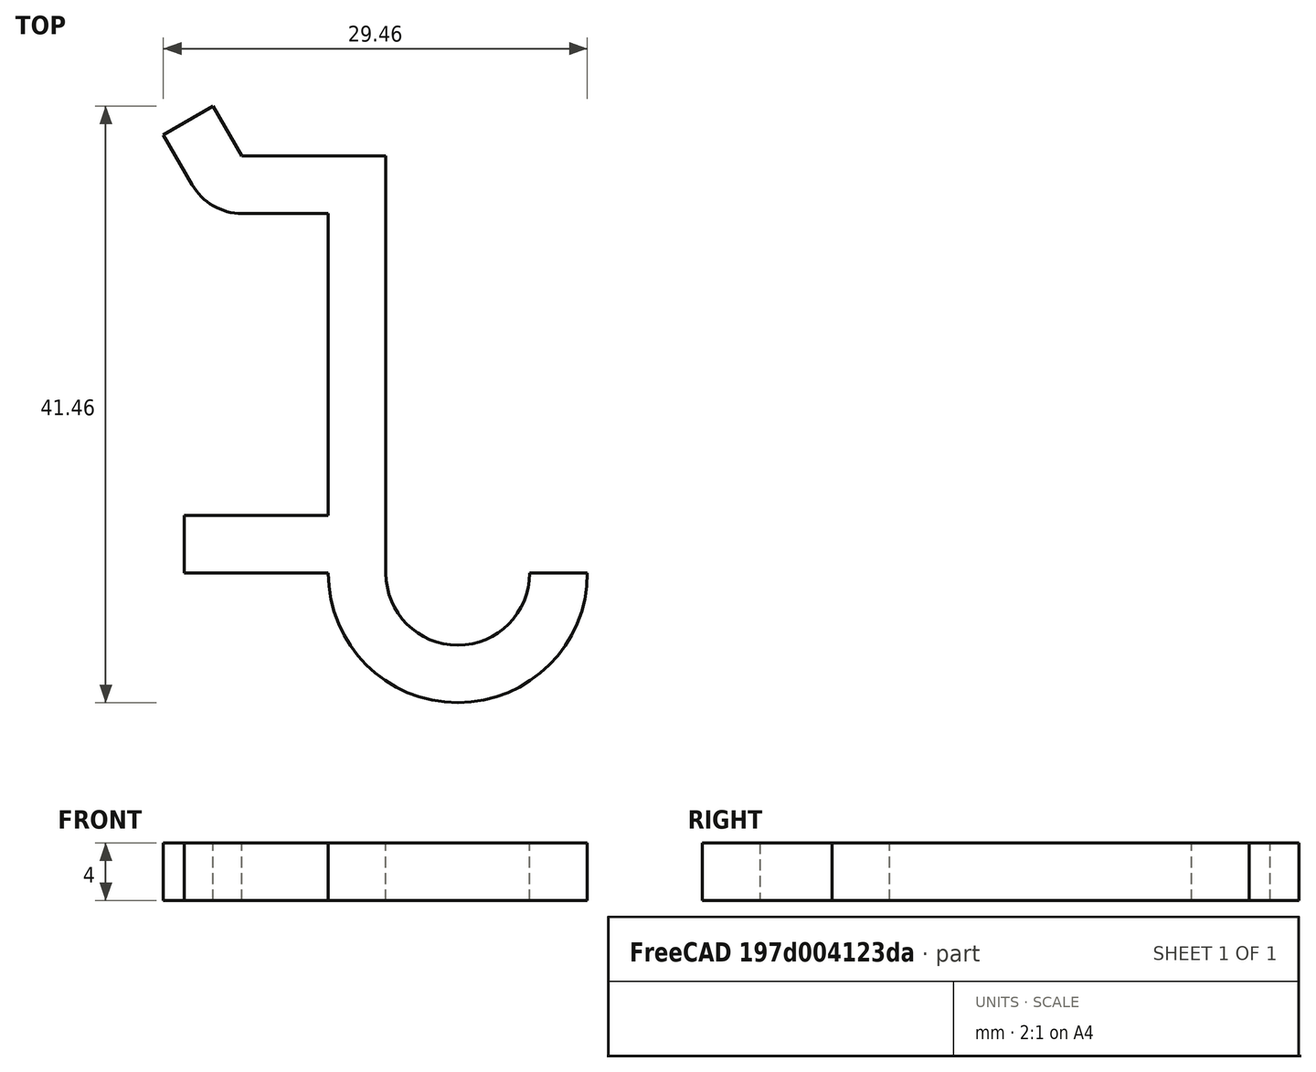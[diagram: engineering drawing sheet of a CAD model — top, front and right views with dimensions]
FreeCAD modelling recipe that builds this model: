
FCSTD DOCUMENT  (FreeCAD 0.18R16146 (Git))
Label: peg
License: All rights reserved
LicenseURL: http://en.wikipedia.org/wiki/All_rights_reserved
objects: Sketcher::SketchObject×1, PartDesign::Pad×1, PartDesign::Body×1, Spreadsheet::Sheet×1
note: 4 computed .brp shape members not serialized (recipe doc carries the construction recipe); baked Part::Feature solids carry a one-line shape summary decoded from their .brp

FEATURE [Sketcher::SketchObject] Sketch
  MapMode = 5
  Support = -> [XY_Plane]
  expr: Constraints[41] = Dimensions.pegdiameter
  sketch-geometry (14):
    g0: LineSegment StartX=-5 StartY=29 StartZ=0 EndX=-5 EndY=0 EndZ=0
    g1: LineSegment StartX=-5 StartY=29 StartZ=0 EndX=-15 EndY=29 EndZ=0
    g2: LineSegment StartX=-15 StartY=25 StartZ=0 EndX=-9 EndY=25 EndZ=0
    g3: LineSegment StartX=-9 StartY=25 StartZ=0 EndX=-9 EndY=4 EndZ=0
    g4: LineSegment StartX=-9 StartY=4 StartZ=0 EndX=-19 EndY=4 EndZ=0
    g5: LineSegment StartX=-19 StartY=4 StartZ=0 EndX=-19 EndY=0 EndZ=0
    g6: LineSegment StartX=-19 StartY=0 StartZ=0 EndX=-9 EndY=0 EndZ=0
    g7: LineSegment StartX=-15 StartY=29 StartZ=0 EndX=-17 EndY=32.4641 EndZ=0
    g8: LineSegment StartX=-17 StartY=32.4641 StartZ=0 EndX=-20.4641 EndY=30.4641 EndZ=0
    g9: LineSegment StartX=-20.4641 StartY=30.4641 StartZ=0 EndX=-18.4641 EndY=27 EndZ=0
    g10: ArcOfCircle CenterX=-15 CenterY=29 CenterZ=0 NormalX=0 NormalY=0 NormalZ=1 AngleXU=0 Radius=4 StartAngle=3.66519 EndAngle=4.71239
    g11: ArcOfCircle CenterX=0 CenterY=0 CenterZ=0 NormalX=0 NormalY=0 NormalZ=1 AngleXU=0 Radius=5 StartAngle=3.14159 EndAngle=6.28319
    g12: ArcOfCircle CenterX=0 CenterY=0 CenterZ=0 NormalX=0 NormalY=0 NormalZ=1 AngleXU=0 Radius=9 StartAngle=3.14159 EndAngle=6.28319
    g13: LineSegment StartX=5 StartY=0 StartZ=0 EndX=9 EndY=0 EndZ=0
  constraints (42):
    c: Vertical(g0)
    c: Horizontal(g1)
    c: Horizontal(g2)
    c: Vertical(g3)
    c: Horizontal(g4)
    c: Vertical(g5)
    c: Horizontal(g6)
    c: Coincident(g3,g2)
    c: Coincident(g4,g3)
    c: Coincident(g5,g4)
    c: Coincident(g6,g5)
    c: DistanceY(g2,g1) = 4
    c: DistanceY(g5,g4) = 4
    c: Coincident(g1,g0)
    c: Coincident(g10,g2)
    c: Coincident(g10,g9)
    c: Coincident(g9,g8)
    c: Coincident(g7,g8)
    c: Coincident(g1,g7)
    c: Coincident(g1,g10)
    c: Radius(g10) = 4
    c: DistanceX(g3,g6) = 0
    c: DistanceX(g2,g0) = 4
    c: DistanceX(g2,g2) = 6
    c: Coincident(g0,g11)
    c: Coincident(g12,g11)
    c: DistanceY(g12,g11) = 0
    c: DistanceY(g0,g6) = 0
    c: Coincident(g12,g6)
    c: Coincident(g13,g11)
    c: Coincident(g13,g12)
    c: DistanceY(g11,g11) = 0
    c: DistanceY(g0,g11) = 0
    c: DistanceY(g3,g2) = 21
    c: Coincident(g11,g-1)
    c: Angle(g1,g7) = 2.0944
    c: Angle(g8,g7) = 1.5708
    c: Distance(g8) = 4
    c: Angle(g9,g8) = 1.5708
    c: Distance(g7) = 4
    c: DistanceX(g5,g6) = 10
    c: Diameter(g11) = 10
FEATURE [PartDesign::Pad] Pad
  Length = 4
  Length2 = 100
  Profile = -> Sketch
  Type = 0
FEATURE [PartDesign::Body] Body
  Group = -> [Sketch,Pad]
  Origin = -> Origin
  Tip = -> Pad
FEATURE [Spreadsheet::Sheet] Spreadsheet  label="Dimensions"
  cells = A1=Peg Diameter (set to 10, 20 or 30); B1(pegdiameter)=10
